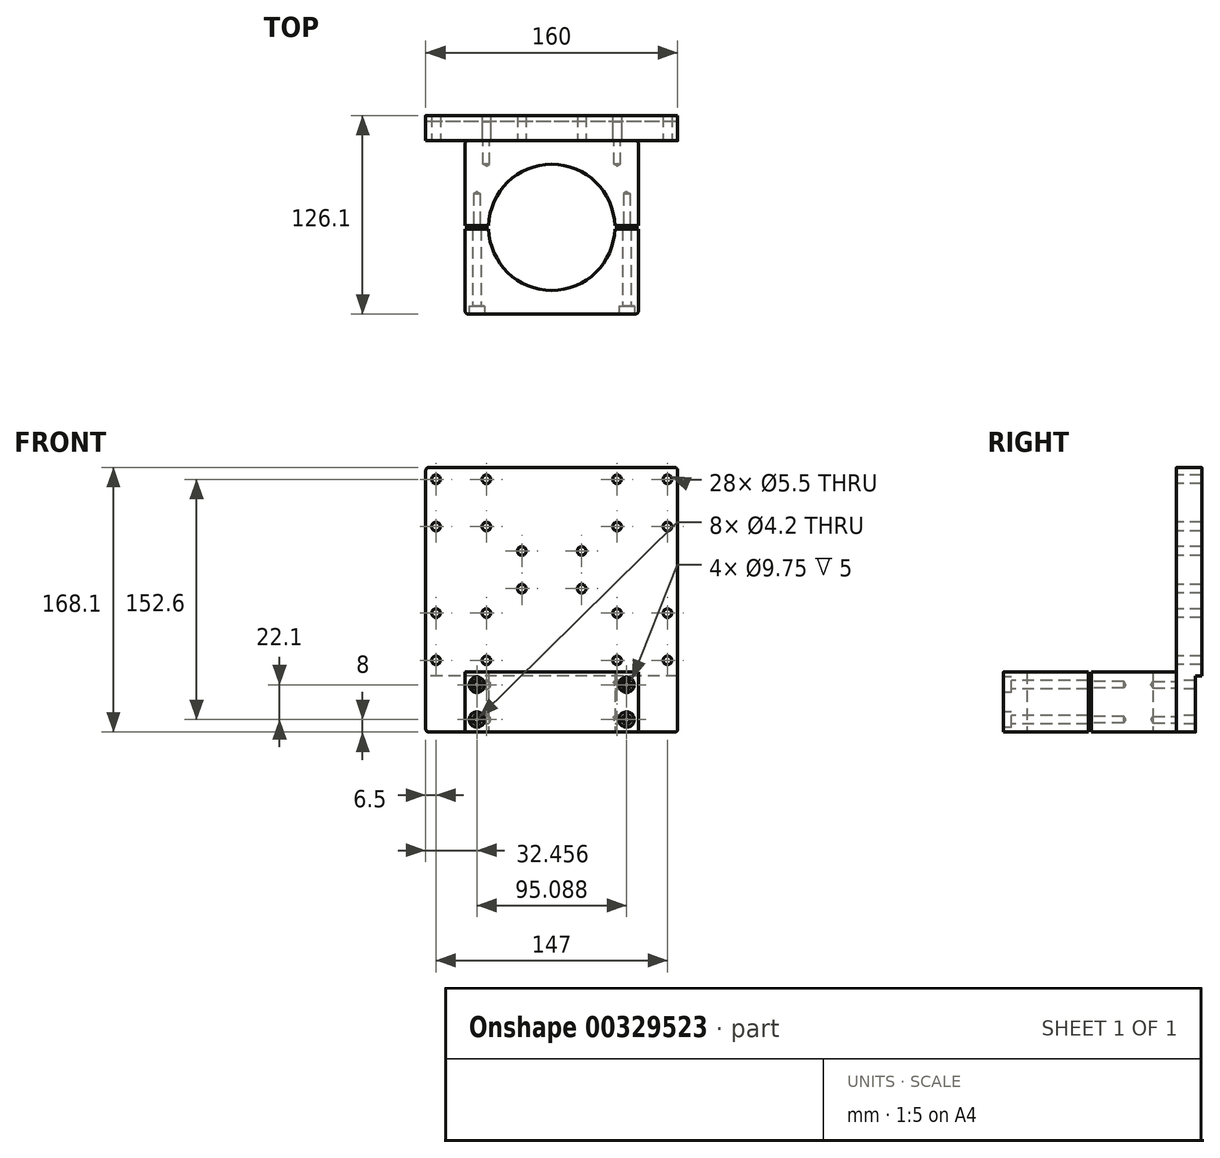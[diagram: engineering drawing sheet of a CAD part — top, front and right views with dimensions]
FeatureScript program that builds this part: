
annotation { "Feature Type Name" : "Feature", "Feature Type Description" : "" }
export const myFeature = defineFeature(function(context is Context, id is Id, definition is map)
    precondition{}
    {
        {
            var Q0;
            Q0=qCreatedBy(makeId("Top.planeOp"),FACE);
            var sketch = newSketch(context, id + "F0", { "sketchPlane" : qUnion([Q0])});
            skArc(sketch, "E0", {"start": v(40.04, 1) * mm, "mid": v(0, 40.05) * mm, "end": v(-40.04, 1) * mm});
            skLineSegment(sketch, "E1.bottom", {"start": v(53.05, 55.05) * mm, "end": v(-53.05, 55.05) * mm});
            skLineSegment(sketch, "E1.top", {"start": v(53.05, -55.05) * mm, "end": v(-53.05, -55.05) * mm});
            skLineSegment(sketch, "E1.left", {"start": v(55.05, 53.05) * mm, "end": v(55.05, 1) * mm});
            skLineSegment(sketch, "E1.right", {"start": v(-55.05, 53.05) * mm, "end": v(-55.05, 1) * mm});
            skPoint(sketch, "E2.visualSharp", {"position": v(-55.05, 55.05) * mm});
            skArc(sketch, "E2.filletArc", {"start": v(-53.05, 55.05) * mm, "mid": v(-54.46, 54.46) * mm, "end": v(-55.05, 53.05) * mm});
            skPoint(sketch, "E3.visualSharp", {"position": v(55.05, 55.05) * mm});
            skArc(sketch, "E3.filletArc", {"start": v(55.05, 53.05) * mm, "mid": v(54.46, 54.46) * mm, "end": v(53.05, 55.05) * mm});
            skPoint(sketch, "E4.visualSharp", {"position": v(-55.05, -55.05) * mm});
            skArc(sketch, "E4.filletArc", {"start": v(-55.05, -53.05) * mm, "mid": v(-54.46, -54.46) * mm, "end": v(-53.05, -55.05) * mm});
            skPoint(sketch, "E5.visualSharp", {"position": v(55.05, -55.05) * mm});
            skArc(sketch, "E5.filletArc", {"start": v(53.05, -55.05) * mm, "mid": v(54.46, -54.46) * mm, "end": v(55.05, -53.05) * mm});
            skLineSegment(sketch, "E6", {"start": v(-55.05, 1) * mm, "end": v(-40.04, 1) * mm});
            skLineSegment(sketch, "E7", {"start": v(-55.05, -1) * mm, "end": v(-40.04, -1) * mm});
            skLineSegment(sketch, "E8.trimOffspring", {"start": v(55.05, -1) * mm, "end": v(55.05, -53.05) * mm});
            skLineSegment(sketch, "E9.trimOffspring", {"start": v(-55.05, -1) * mm, "end": v(-55.05, -53.05) * mm});
            skArc(sketch, "E10.trimOffspring", {"start": v(-40.04, -1) * mm, "mid": v(0, -40.05) * mm, "end": v(40.04, -1) * mm});
            skLineSegment(sketch, "E11.trimOffspring", {"start": v(40.04, -1) * mm, "end": v(55.05, -1) * mm});
            skLineSegment(sketch, "E12.trimOffspring", {"start": v(40.04, 1) * mm, "end": v(55.05, 1) * mm});
            skSolve(sketch);
        }
        {
            var Q0;
            Q0 = qSketchRegion(id + "F0", true);
            extrude(context, id + "F1", {"entities" : qUnion([Q0]), "endBound" : BoundingType.SYMMETRIC, "depth" : 38.1 * mm});
        }
        {
            var Q0;
            Q0=makeQuery(id+"F1.opExtrude","SWEPT_FACE",FACE,{"disambiguationData":[OSD([sQuery(id+"F0.wireOp",EDGE,"E1.bottom")])]});
            var sketch = newSketch(context, id + "F2", { "sketchPlane" : qUnion([Q0])});
            skLineSegment(sketch, "E13.bottom", {"start": v(-78, 149.05) * mm, "end": v(78, 149.05) * mm});
            skLineSegment(sketch, "E13.top", {"start": v(-78, -19.05) * mm, "end": v(78, -19.05) * mm});
            skLineSegment(sketch, "E13.left", {"start": v(-80, 147.05) * mm, "end": v(-80, -17.05) * mm});
            skLineSegment(sketch, "E13.right", {"start": v(80, 147.05) * mm, "end": v(80, -17.05) * mm});
            skPoint(sketch, "E14", {"position": v(0, -19.05) * mm});
            skPoint(sketch, "E15.visualSharp", {"position": v(-80, -19.05) * mm});
            skArc(sketch, "E15.filletArc", {"start": v(-80, -17.05) * mm, "mid": v(-79.41, -18.46) * mm, "end": v(-78, -19.05) * mm});
            skPoint(sketch, "E16.visualSharp", {"position": v(-80, 149.05) * mm});
            skArc(sketch, "E16.filletArc", {"start": v(-78, 149.05) * mm, "mid": v(-79.41, 148.46) * mm, "end": v(-80, 147.05) * mm});
            skPoint(sketch, "E17.visualSharp", {"position": v(80, 149.05) * mm});
            skArc(sketch, "E17.filletArc", {"start": v(80, 147.05) * mm, "mid": v(79.41, 148.46) * mm, "end": v(78, 149.05) * mm});
            skPoint(sketch, "E18.visualSharp", {"position": v(80, -19.05) * mm});
            skArc(sketch, "E18.filletArc", {"start": v(78, -19.05) * mm, "mid": v(79.41, -18.46) * mm, "end": v(80, -17.05) * mm});
            skCircle(sketch, "E19", {"center": v(-73.5, 141.55) * mm, "radius": 2.75 * mm});
            skCircle(sketch, "E20", {"center": v(-41.5, 141.55) * mm, "radius": 2.75 * mm});
            skCircle(sketch, "E21", {"center": v(-73.5, 111.55) * mm, "radius": 2.75 * mm});
            skCircle(sketch, "E22", {"center": v(-41.5, 111.55) * mm, "radius": 2.75 * mm});
            skCircle(sketch, "E23", {"center": v(41.5, 141.55) * mm, "radius": 2.75 * mm});
            skCircle(sketch, "E24", {"center": v(73.5, 141.55) * mm, "radius": 2.75 * mm});
            skCircle(sketch, "E25", {"center": v(41.5, 111.55) * mm, "radius": 2.75 * mm});
            skCircle(sketch, "E26", {"center": v(73.5, 111.55) * mm, "radius": 2.75 * mm});
            skCircle(sketch, "E27", {"center": v(-73.5, 56.55) * mm, "radius": 2.75 * mm});
            skCircle(sketch, "E28", {"center": v(-73.5, 26.55) * mm, "radius": 2.75 * mm});
            skCircle(sketch, "E29", {"center": v(-41.5, 26.55) * mm, "radius": 2.75 * mm});
            skCircle(sketch, "E30", {"center": v(-41.5, 56.55) * mm, "radius": 2.75 * mm});
            skCircle(sketch, "E31", {"center": v(41.5, 56.55) * mm, "radius": 2.75 * mm});
            skCircle(sketch, "E32", {"center": v(73.5, 56.55) * mm, "radius": 2.75 * mm});
            skCircle(sketch, "E33", {"center": v(41.5, 26.55) * mm, "radius": 2.75 * mm});
            skCircle(sketch, "E34", {"center": v(73.5, 26.55) * mm, "radius": 2.75 * mm});
            skCircle(sketch, "E35", {"center": v(-19, 96.05) * mm, "radius": 2.75 * mm});
            skCircle(sketch, "E36", {"center": v(19, 96.05) * mm, "radius": 2.75 * mm});
            skCircle(sketch, "E37", {"center": v(-19, 72.05) * mm, "radius": 2.75 * mm});
            skCircle(sketch, "E38", {"center": v(19, 72.05) * mm, "radius": 2.75 * mm});
            skLineSegment(sketch, "E39", {"start": v(19, 96.05) * mm, "end": v(19, 72.05) * mm, "construction": true});
            skLineSegment(sketch, "E40", {"start": v(41.5, 111.55) * mm, "end": v(41.5, 56.55) * mm, "construction": true});
            skPoint(sketch, "E41", {"position": v(41.5, 84.05) * mm});
            skPoint(sketch, "E42", {"position": v(19, 84.05) * mm});
            skLineSegment(sketch, "E43.bottom", {"start": v(41.5, 11.05) * mm, "end": v(-41.5, 11.05) * mm, "construction": true});
            skLineSegment(sketch, "E43.top", {"start": v(41.5, -11.05) * mm, "end": v(-41.5, -11.05) * mm, "construction": true});
            skLineSegment(sketch, "E43.left", {"start": v(41.5, 11.05) * mm, "end": v(41.5, -11.05) * mm, "construction": true});
            skLineSegment(sketch, "E43.right", {"start": v(-41.5, 11.05) * mm, "end": v(-41.5, -11.05) * mm, "construction": true});
            skPoint(sketch, "E43.middle", {"position": v(0, 0) * mm});
            skCircle(sketch, "E44", {"center": v(-41.5, 11.05) * mm, "radius": 2.75 * mm});
            skCircle(sketch, "E45", {"center": v(-41.5, -11.05) * mm, "radius": 2.75 * mm});
            skCircle(sketch, "E46", {"center": v(41.5, -11.05) * mm, "radius": 2.75 * mm});
            skCircle(sketch, "E47", {"center": v(41.5, 11.05) * mm, "radius": 2.75 * mm});
            skSolve(sketch);
        }
        {
            var Q0;
            Q0 = qSketchRegion(id + "F2", true);
            extrude(context, id + "F3", {"entities" : qUnion([Q0]), "depth" : 16 * mm});
        }
        {
            var Q0;
            Q0=makeQuery(id+"F1.opExtrude","SWEPT_FACE",FACE,{"disambiguationData":[OSD([sQuery(id+"F0.wireOp",EDGE,"E1.top")])]});
            var sketch = newSketch(context, id + "F4", { "sketchPlane" : qUnion([Q0])});
            skPoint(sketch, "E48", {"position": v(-47.54, 11.05) * mm});
            skPoint(sketch, "E49", {"position": v(-47.54, -11.05) * mm});
            skPoint(sketch, "E50", {"position": v(47.54, 11.05) * mm});
            skPoint(sketch, "E51", {"position": v(47.54, -11.05) * mm});
            skSolve(sketch);
        }
        {
            var Q0;
            Q0=sQuery(id+"F4.wireOp",VERTEX,"E48");
            var Q1;
            Q1=sQuery(id+"F4.wireOp",VERTEX,"E49");
            var Q2;
            Q2=sQuery(id+"F4.wireOp",VERTEX,"E50");
            var Q3;
            Q3=sQuery(id+"F4.wireOp",VERTEX,"E51");
            var Q4;
            Q4=makeQuery(id+"F1.opExtrude","SWEPT_BODY",BODY,{"disambiguationData":[OSD([sQuery(id+"F0.wireOp",EDGE,"E1.top"),sQuery(id+"F0.wireOp",EDGE,"E4.filletArc"),sQuery(id+"F0.wireOp",EDGE,"E5.filletArc"),sQuery(id+"F0.wireOp",EDGE,"E7"),sQuery(id+"F0.wireOp",EDGE,"E8.trimOffspring"),sQuery(id+"F0.wireOp",EDGE,"E9.trimOffspring"),sQuery(id+"F0.wireOp",EDGE,"E10.trimOffspring"),sQuery(id+"F0.wireOp",EDGE,"E11.trimOffspring")])]});
            hole(context, id + "F5", {"style" : HoleStyle.C_BORE, "endStyle" : HoleEndStyle.THROUGH, "standardTappedOrClearance" : lookupTablePath({ "standard" : "ISO", "fit" : "Normal", "size" : "M5", "type" : "Clearance" }), "standardBlindInLast" : lookupTablePath({ "fit" : "Standard", "standard" : "ISO", "size" : "M5", "type" : "Clearance" }), "holeDiameter" : 5.5 * mm, "cBoreDiameter" : 9.75 * mm, "cBoreDepth" : 5 * mm, "tappedDepth" : 18 * mm, "tapClearance" : 3, "locations" : qUnion([Q0, Q1, Q2, Q3]), "scope" : qUnion([Q4])});
        }
        {
            var Q0;
            Q0=makeQuery(id+"F1.opExtrude","SWEPT_FACE",FACE,{"disambiguationData":[OSD([sQuery(id+"F0.wireOp",EDGE,"E1.bottom")])]});
            var sketch = newSketch(context, id + "F6", { "sketchPlane" : qUnion([Q0])});
            skPoint(sketch, "E52", {"position": v(-41.5, 11.05) * mm});
            skPoint(sketch, "E53", {"position": v(41.5, 11.05) * mm});
            skPoint(sketch, "E54", {"position": v(41.5, -11.05) * mm});
            skPoint(sketch, "E55", {"position": v(-41.5, -11.05) * mm});
            skSolve(sketch);
        }
        {
            var Q0;
            Q0=sQuery(id+"F6.wireOp",VERTEX,"E55");
            var Q1;
            Q1=sQuery(id+"F6.wireOp",VERTEX,"E52");
            var Q2;
            Q2=sQuery(id+"F6.wireOp",VERTEX,"E53");
            var Q3;
            Q3=sQuery(id+"F6.wireOp",VERTEX,"E54");
            var Q4;
            Q4=makeQuery(id+"F1.opExtrude","SWEPT_BODY",BODY,{"disambiguationData":[OSD([sQuery(id+"F0.wireOp",EDGE,"E0"),sQuery(id+"F0.wireOp",EDGE,"E1.bottom"),sQuery(id+"F0.wireOp",EDGE,"E1.left"),sQuery(id+"F0.wireOp",EDGE,"E1.right"),sQuery(id+"F0.wireOp",EDGE,"E2.filletArc"),sQuery(id+"F0.wireOp",EDGE,"E3.filletArc"),sQuery(id+"F0.wireOp",EDGE,"E6"),sQuery(id+"F0.wireOp",EDGE,"E12.trimOffspring")])]});
            hole(context, id + "F7", {"style" : HoleStyle.SIMPLE, "endStyle" : HoleEndStyle.BLIND, "standardTappedOrClearance" : lookupTablePath({ "standard" : "ISO", "engagement" : "75%", "pitch" : "0.8 mm", "size" : "M5", "type" : "Tapped" }), "standardBlindInLast" : lookupTablePath({ "standard" : "ISO", "engagement" : "75%", "pitch" : "0.8 mm", "size" : "M5", "type" : "Tapped" }), "holeDiameter" : 4.2 * mm, "showTappedDepth" : true, "holeDepth" : 15 * mm, "tappedDepth" : 12.6 * mm, "tapClearance" : 3, "locations" : qUnion([Q0, Q1, Q2, Q3]), "scope" : qUnion([Q4]), "majorDiameter" : 5 * mm});
        }
        {
            var Q0;
            Q0=makeQuery(id+"F1.opExtrude","SWEPT_FACE",FACE,{"disambiguationData":[OSD([sQuery(id+"F0.wireOp",EDGE,"E6")])]});
            var sketch = newSketch(context, id + "F8", { "sketchPlane" : qUnion([Q0])});
            skPoint(sketch, "E56", {"position": v(-47.54, 11.05) * mm});
            skPoint(sketch, "E57", {"position": v(47.54, 11.05) * mm});
            skPoint(sketch, "E58", {"position": v(47.54, -11.05) * mm});
            skPoint(sketch, "E59", {"position": v(-47.54, -11.05) * mm});
            skSolve(sketch);
        }
        {
            var Q0;
            Q0=sQuery(id+"F8.wireOp",VERTEX,"E56");
            var Q1;
            Q1=sQuery(id+"F8.wireOp",VERTEX,"E59");
            var Q2;
            Q2=sQuery(id+"F8.wireOp",VERTEX,"E58");
            var Q3;
            Q3=sQuery(id+"F8.wireOp",VERTEX,"E57");
            var Q4;
            Q4=makeQuery(id+"F1.opExtrude","SWEPT_BODY",BODY,{"disambiguationData":[OSD([sQuery(id+"F0.wireOp",EDGE,"E0"),sQuery(id+"F0.wireOp",EDGE,"E1.bottom"),sQuery(id+"F0.wireOp",EDGE,"E1.left"),sQuery(id+"F0.wireOp",EDGE,"E1.right"),sQuery(id+"F0.wireOp",EDGE,"E2.filletArc"),sQuery(id+"F0.wireOp",EDGE,"E3.filletArc"),sQuery(id+"F0.wireOp",EDGE,"E6"),sQuery(id+"F0.wireOp",EDGE,"E12.trimOffspring")])]});
            hole(context, id + "F9", {"style" : HoleStyle.SIMPLE, "endStyle" : HoleEndStyle.BLIND, "standardTappedOrClearance" : lookupTablePath({ "standard" : "ISO", "engagement" : "75%", "pitch" : "0.8 mm", "size" : "M5", "type" : "Tapped" }), "standardBlindInLast" : lookupTablePath({ "standard" : "ISO", "engagement" : "75%", "pitch" : "0.8 mm", "size" : "M5", "type" : "Tapped" }), "holeDiameter" : 4.2 * mm, "showTappedDepth" : true, "holeDepth" : 20.4 * mm, "tappedDepth" : 18 * mm, "tapClearance" : 3, "locations" : qUnion([Q0, Q1, Q2, Q3]), "scope" : qUnion([Q4]), "majorDiameter" : 5 * mm});
        }
        {
            var Q0;
            Q0=makeQuery(id+"F3.opExtrude","CAP_FACE",FACE,{"disambiguationData":[OSD([sQuery(id+"F2.wireOp",EDGE,"E13.bottom"),sQuery(id+"F2.wireOp",EDGE,"E13.top"),sQuery(id+"F2.wireOp",EDGE,"E13.left"),sQuery(id+"F2.wireOp",EDGE,"E13.right"),sQuery(id+"F2.wireOp",EDGE,"E15.filletArc"),sQuery(id+"F2.wireOp",EDGE,"E16.filletArc"),sQuery(id+"F2.wireOp",EDGE,"E17.filletArc"),sQuery(id+"F2.wireOp",EDGE,"E18.filletArc"),sQuery(id+"F2.wireOp",EDGE,"E19"),sQuery(id+"F2.wireOp",EDGE,"E20"),sQuery(id+"F2.wireOp",EDGE,"E21"),sQuery(id+"F2.wireOp",EDGE,"E22"),sQuery(id+"F2.wireOp",EDGE,"E23"),sQuery(id+"F2.wireOp",EDGE,"E24"),sQuery(id+"F2.wireOp",EDGE,"E25"),sQuery(id+"F2.wireOp",EDGE,"E26"),sQuery(id+"F2.wireOp",EDGE,"E27"),sQuery(id+"F2.wireOp",EDGE,"E28"),sQuery(id+"F2.wireOp",EDGE,"E29"),sQuery(id+"F2.wireOp",EDGE,"E30"),sQuery(id+"F2.wireOp",EDGE,"E31"),sQuery(id+"F2.wireOp",EDGE,"E32"),sQuery(id+"F2.wireOp",EDGE,"E33"),sQuery(id+"F2.wireOp",EDGE,"E34"),sQuery(id+"F2.wireOp",EDGE,"E35"),sQuery(id+"F2.wireOp",EDGE,"E36"),sQuery(id+"F2.wireOp",EDGE,"E37"),sQuery(id+"F2.wireOp",EDGE,"E38"),sQuery(id+"F2.wireOp",EDGE,"E44"),sQuery(id+"F2.wireOp",EDGE,"E45"),sQuery(id+"F2.wireOp",EDGE,"E46"),sQuery(id+"F2.wireOp",EDGE,"E47")])],"isStart":false});
            var sketch = newSketch(context, id + "F10", { "sketchPlane" : qUnion([Q0])});
            skLineSegment(sketch, "E60.bottom", {"start": v(-80, 16.55) * mm, "end": v(80, 16.55) * mm});
            skLineSegment(sketch, "E60.top", {"start": v(-80, -19.05) * mm, "end": v(80, -19.05) * mm});
            skLineSegment(sketch, "E60.left", {"start": v(-80, 16.55) * mm, "end": v(-80, -19.05) * mm});
            skLineSegment(sketch, "E60.right", {"start": v(80, 16.55) * mm, "end": v(80, -19.05) * mm});
            skPoint(sketch, "E61", {"position": v(73.5, 26.55) * mm});
            skSolve(sketch);
        }
        {
            var Q0;
            Q0 = qSketchRegion(id + "F10", true);
            extrude(context, id + "F11", {"entities" : qUnion([Q0]), "operationType" : NewBodyOperationType.REMOVE, "oppositeDirection" : true, "depth" : 4 * mm});
        }
    });
